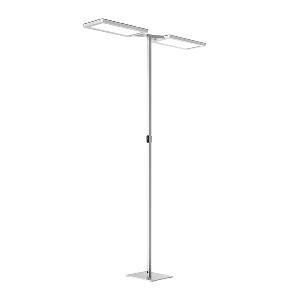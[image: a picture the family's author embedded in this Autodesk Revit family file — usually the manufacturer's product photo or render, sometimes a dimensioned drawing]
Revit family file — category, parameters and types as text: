
# Revit family: yara_doublet_-_yts_2_12000_840_r_sr_cee_00_c_114268000-00810707_baa3
name_source: partatom
category: Lighting Fixtures
units: mm (PartAtom-declared; Revit-internal decimal feet)

## family parameters
Cut with Voids When Loaded = No
Host = Face
Light Source = No
Part Type = Normal
Room Calculation Point = No
Round Connector Dimension = Use Diameter
Shared = No

## types (1)
- YARA.doubleT - YTS 2/12000/840/R/SR/CEE/00/C (1 x LED, 12000 lm, 4000K)
    Apparent Load = 168 VA
    Approval mark = CE
    CIE Flux Codes = 58 87 97 13 100
    Color Rendering = 80-89
    Color Temperature = 4000K
    Control Gear = Electronic ballast
    Default Elevation = 1800 mm
    Description = YTS 2/12000/840/R/SR/CEE/00/R|Free-standing luminaire|light source: LED|work equipment: Electronic ballast DALI|connected load: 220-240 V, 50/60 Hz|Power consumption: approx. 166 W|power factor: approx. 0,966|luminous flux: 24000 lm|luminous efficacy: 144 lm/W|light distribution: Direct/indirect|direct ratio: approx. 13 %|colour temperature: Cold white, ca. 4000 K|color rendering index (CRI): >= 80|chromaticity tolerance:  3 SDCM|technology: Presence and daylight sensor control (PIR)|operation: Wireless switch|luminaire body|material: Aluminium/plastic|surface: Powder coatet|colour: Silver metallic|lamp cover: Acrylic (PMMA), Satine, Structured|tubular section|material: Steel tube|surface: Powder-coated|Form: Tubular section upright|colour of tubular section: Silver metallic|luminaire base|Form: Rectangular flat|weight (net): approx. 24.0 kg|mains lead: 3.00 m Mains plug CEE 7/VII|Fastening: Floor standing base|glare control: Conical prismatic screen|luminance(L65): <= 2200 cd/m|unified glare rating(4H 8H): <=  16|special features: App control, Asymmetric radiation, Direct and indirect lighting component with edge light and light guidetechnology for a homogeneous light exit, Flicker-free, Magnetic control panel, freely positionable, PIR movement and daylight sensor|Approval mark: VDE - ENEC|
    Frequency = 50 Hz, 60 Hz
    Height = 24 mm  [stored 0.0787402 ft]
    Lamp = 1 x LED
    Lamp Light Flux = 12000 lm
    Lamp count = 1
    Length = 690 mm
    Luminous efficacy = 143 lm/W
    Manufacturer = Waldmann
    ModVariant = No
    Model = 114268000-00810707
    Mounting Place = Floor
    Mounting Type = Freestanding
    Number of Poles = 1
    OnlyDefault = Yes
    Power Factor = 1
    Product Name = YARA.doubleT - YTS 2/12000/840/R/SR/CEE/00/C
    Product group = Free standing luminaire
    ProductGroupID = 13
    Protection Class = Protection class I
    Protection Degree = IP 20
    RLX_Detail_Level = 1
    RlxData = <blob elided: 63277 chars, md5=f27c962a>
    Socket = socket
    Standby Power = 0 W
    System Light Flux = 24000 lm
    System Power = 168 W
    Type Comments = Product without accessories
    Type Image = yts-r-sr-r.jpg
    URL = http://relux.com
    VarID = ---
    Voltage = 230 V
    Voltage Range = 220-240 V
    Weight = 0.00 kg
    Width = 358 mm

note: [stored X ft] marks values corroborated as IEEE doubles in the binary element streams (Revit-internal decimal feet)

## geometry (parser evidence)
native form markers: Blend x4, Sweep x19
no freeform markers — native parametric forms only
